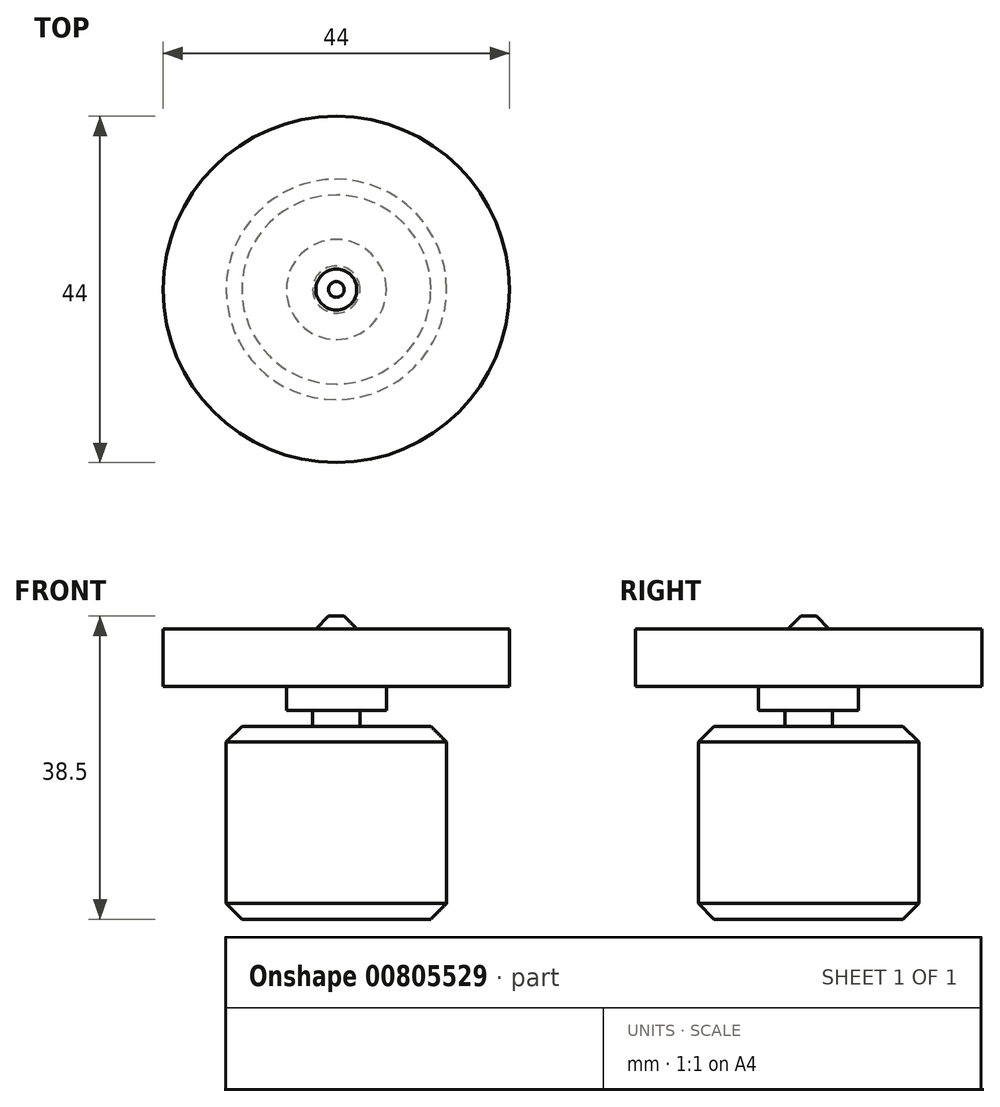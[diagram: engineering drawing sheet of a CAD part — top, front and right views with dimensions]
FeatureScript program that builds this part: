
annotation { "Feature Type Name" : "Feature", "Feature Type Description" : "" }
export const myFeature = defineFeature(function(context is Context, id is Id, definition is map)
    precondition{}
    {
        {
            var Q0;
            Q0=qCreatedBy(makeId("Top.planeOp"),FACE);
            var sketch = newSketch(context, id + "F0", { "sketchPlane" : qUnion([Q0])});
            skCircle(sketch, "E0", {"center": v(0, 0) * mm, "radius": 14 * mm});
            skCircle(sketch, "E1", {"center": v(0, 0) * mm, "radius": 3 * mm});
            skSolve(sketch);
        }
        {
            var Q0;
            Q0=makeQuery(id+"F0.imprint","IMPRINT",FACE,{"disambiguationData":[TD([[makeQuery(id+"F0.imprint","IMPRINT",EDGE,{"derivedFrom":sQuery(id+"F0.wireOp",EDGE,"E1")}),1.0]])]});
            extrude(context, id + "F1", {"entities" : qUnion([Q0]), "depth" : 38.5 * mm, "offsetDistance" : 25 * mm});
        }
        {
            var Q0;
            Q0=makeQuery(id+"F0.imprint","IMPRINT",FACE,{"disambiguationData":[TD([[makeQuery(id+"F0.imprint","IMPRINT",EDGE,{"derivedFrom":sQuery(id+"F0.wireOp",EDGE,"E0")}),1.0]])]});
            extrude(context, id + "F2", {"entities" : qUnion([Q0]), "operationType" : NewBodyOperationType.ADD, "depth" : 24.5 * mm, "offsetDistance" : 25 * mm});
        }
        {
            var Q0;
            Q0=makeQuery(id+"F2.opExtrude","CAP_EDGE",EDGE,{"disambiguationData":[OSD([sQuery(id+"F0.wireOp",EDGE,"E0")])],"isStart":true});
            var Q1;
            Q1=makeQuery(id+"F2.opExtrude","CAP_EDGE",EDGE,{"disambiguationData":[OSD([sQuery(id+"F0.wireOp",EDGE,"E0")])],"isStart":false});
            var Q2;
            Q2=makeQuery(id+"F1.opExtrude","CAP_EDGE",EDGE,{"disambiguationData":[OSD([sQuery(id+"F0.wireOp",EDGE,"E1")])],"isStart":false});
            chamfer(context, id + "F3", {"entities" : qUnion([Q0, Q1, Q2]), "width" : 2 * mm, "tangentPropagation" : true});
        }
        {
            var Q0;
            Q0=makeQuery(id+"F2.opExtrude","CAP_FACE",FACE,{"disambiguationData":[OSD([sQuery(id+"F0.wireOp",EDGE,"E0"),sQuery(id+"F0.wireOp",EDGE,"E1")])],"isStart":false});
            cPlane(context, id + "F4", {"entities" : qUnion([Q0]), "cplaneType" : CPlaneType.OFFSET, "offset" : 5.1 * mm, "width" : 150 * mm, "height" : 150 * mm});
        }
        {
            var Q0;
            Q0=qCreatedBy(id+"F4.planeOp",FACE);
            var sketch = newSketch(context, id + "F5", { "sketchPlane" : qUnion([Q0])});
            skCircle(sketch, "E2", {"center": v(0, 0) * mm, "radius": 22 * mm});
            skCircle(sketch, "E3", {"center": v(0, 0) * mm, "radius": 6.35 * mm});
            skSolve(sketch);
        }
        {
            var Q0;
            Q0=makeQuery(id+"F5.imprint","IMPRINT",FACE,{"disambiguationData":[TD([[makeQuery(id+"F5.imprint","IMPRINT",EDGE,{"derivedFrom":sQuery(id+"F5.wireOp",EDGE,"E2")}),1.0]])]});
            var Q1;
            Q1=makeQuery(id+"F5.imprint","IMPRINT",FACE,{"disambiguationData":[TD([[makeQuery(id+"F5.imprint","IMPRINT",EDGE,{"derivedFrom":sQuery(id+"F5.wireOp",EDGE,"E3")}),1.0]])]});
            extrude(context, id + "F6", {"entities" : qUnion([Q0, Q1]), "operationType" : NewBodyOperationType.ADD, "depth" : 7.3 * mm, "offsetDistance" : 25 * mm});
        }
        {
            var Q0;
            Q0=makeQuery(id+"F5.imprint","IMPRINT",FACE,{"disambiguationData":[TD([[makeQuery(id+"F5.imprint","IMPRINT",EDGE,{"derivedFrom":sQuery(id+"F5.wireOp",EDGE,"E3")}),1.0]])]});
            extrude(context, id + "F7", {"entities" : qUnion([Q0]), "operationType" : NewBodyOperationType.ADD, "oppositeDirection" : true, "depth" : 3.1 * mm, "offsetDistance" : 25 * mm});
        }
    });
